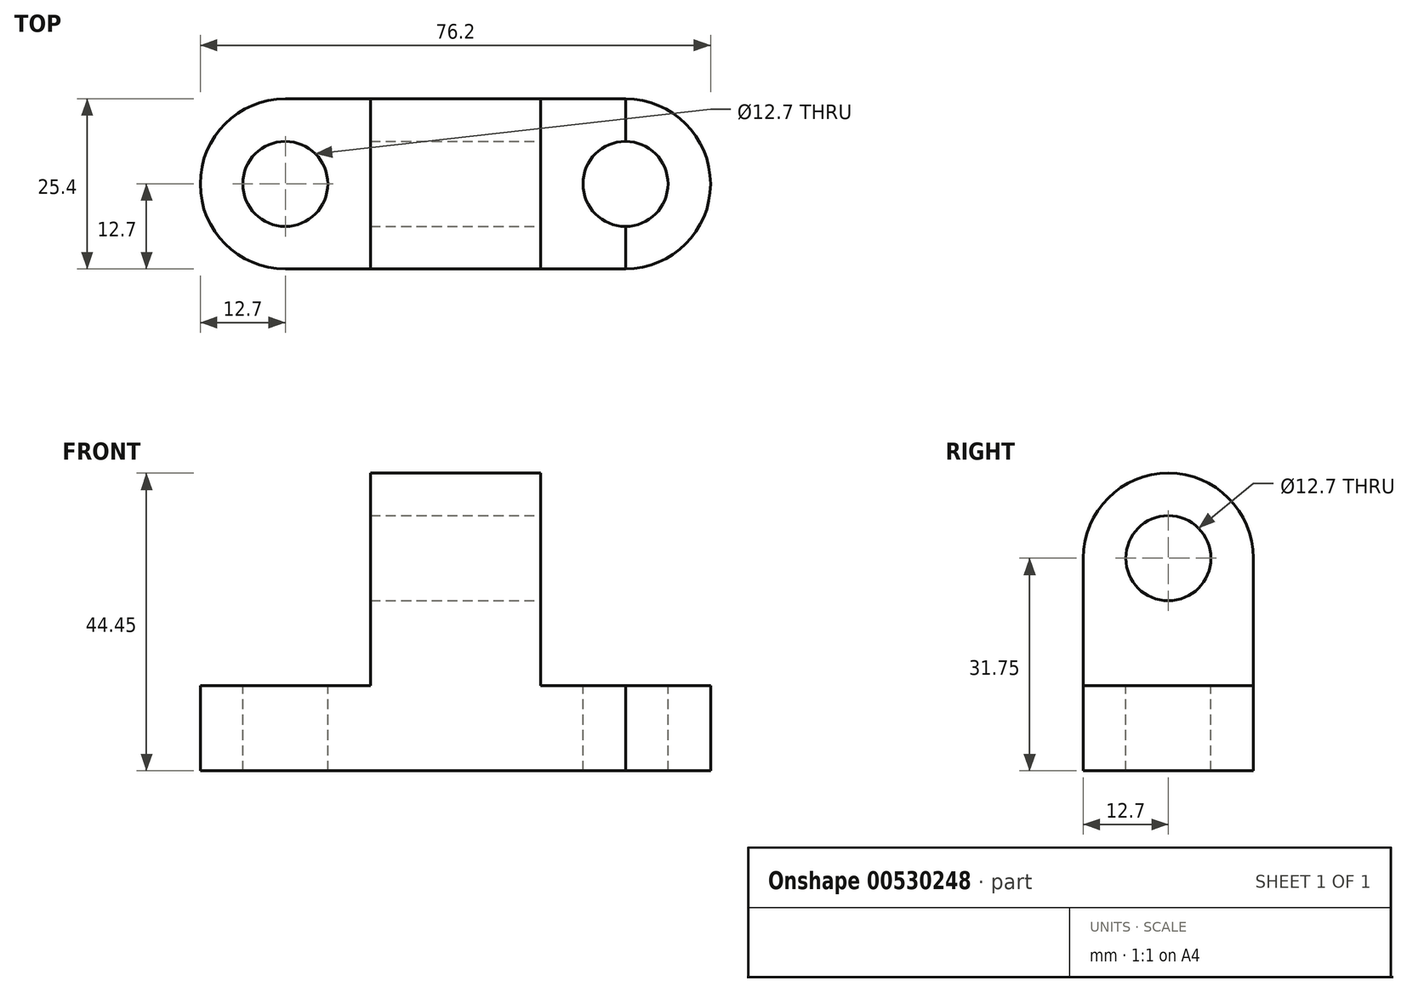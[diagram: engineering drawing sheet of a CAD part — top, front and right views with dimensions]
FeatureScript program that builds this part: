
annotation { "Feature Type Name" : "Feature", "Feature Type Description" : "" }
export const myFeature = defineFeature(function(context is Context, id is Id, definition is map)
    precondition{}
    {
        {
            var Q0;
            Q0=qCreatedBy(makeId("Front.planeOp"),FACE);
            var sketch = newSketch(context, id + "F0", { "sketchPlane" : qUnion([Q0])});
            skLineSegment(sketch, "E0", {"start": v(-77.55, 0) * mm, "end": v(-26.75, 0) * mm});
            skLineSegment(sketch, "E1", {"start": v(-26.75, 0) * mm, "end": v(-26.75, 12.7) * mm});
            skLineSegment(sketch, "E2", {"start": v(-26.75, 12.7) * mm, "end": v(-39.45, 12.7) * mm});
            skLineSegment(sketch, "E3", {"start": v(-39.45, 12.7) * mm, "end": v(-39.45, 31.75) * mm});
            skLineSegment(sketch, "E4", {"start": v(-39.45, 31.75) * mm, "end": v(-64.85, 31.75) * mm});
            skLineSegment(sketch, "E5", {"start": v(-64.85, 31.75) * mm, "end": v(-64.85, 12.7) * mm});
            skLineSegment(sketch, "E6", {"start": v(-64.85, 12.7) * mm, "end": v(-77.55, 12.7) * mm});
            skLineSegment(sketch, "E7", {"start": v(-77.55, 12.7) * mm, "end": v(-77.55, 0) * mm});
            skSolve(sketch);
        }
        {
            var Q0;
            Q0 = qSketchRegion(id + "F0", true);
            extrude(context, id + "F1", {"entities" : qUnion([Q0]), "depth" : 25.4 * mm, "offsetDistance" : 25.4 * mm});
        }
        {
            var Q0;
            Q0=makeQuery(id+"F1.opExtrude","SWEPT_FACE",FACE,{"disambiguationData":[OSD([sQuery(id+"F0.wireOp",EDGE,"E2")])]});
            var sketch = newSketch(context, id + "F2", { "sketchPlane" : qUnion([Q0])});
            skArc(sketch, "E8", {"start": v(-26.75, -25.4) * mm, "mid": v(-14.05, -12.7) * mm, "end": v(-26.75, 0) * mm});
            skSolve(sketch);
        }
        {
            var Q0;
            Q0 = qSketchRegion(id + "F2", true);
            var Q1;
            Q1=makeQuery(id+"F2.imprint","IMPRINT",FACE,{"disambiguationData":[TD([[makeQuery(id+"F2.imprint","IMPRINT",EDGE,{"derivedFrom":sQuery(id+"F2.wireOp",EDGE,"E8")}),1.0]])]});
            extrude(context, id + "F3", {"entities" : qUnion([Q0, Q1]), "oppositeDirection" : true, "depth" : 12.7 * mm, "offsetDistance" : 25.4 * mm});
        }
        {
            var Q0;
            Q0=makeQuery(id+"F1.opExtrude","SWEPT_FACE",FACE,{"disambiguationData":[OSD([sQuery(id+"F0.wireOp",EDGE,"E6")])]});
            var sketch = newSketch(context, id + "F4", { "sketchPlane" : qUnion([Q0])});
            skArc(sketch, "E9", {"start": v(-77.55, 0) * mm, "mid": v(-90.25, -12.7) * mm, "end": v(-77.55, -25.4) * mm});
            skSolve(sketch);
        }
        {
            var Q0;
            Q0 = qSketchRegion(id + "F4", true);
            var Q1;
            Q1=makeQuery(id+"F4.imprint","IMPRINT",FACE,{"disambiguationData":[TD([[makeQuery(id+"F4.imprint","IMPRINT",EDGE,{"derivedFrom":sQuery(id+"F4.wireOp",EDGE,"E9")}),1.0]])]});
            extrude(context, id + "F5", {"entities" : qUnion([Q0, Q1]), "operationType" : NewBodyOperationType.ADD, "oppositeDirection" : true, "depth" : 12.7 * mm, "offsetDistance" : 25.4 * mm});
        }
        {
            var Q0;
            Q0=makeQuery(id+"F1.opExtrude","SWEPT_FACE",FACE,{"disambiguationData":[OSD([sQuery(id+"F0.wireOp",EDGE,"E3")])]});
            var sketch = newSketch(context, id + "F6", { "sketchPlane" : qUnion([Q0])});
            skArc(sketch, "E10", {"start": v(0, 31.75) * mm, "mid": v(-12.7, 44.45) * mm, "end": v(-25.4, 31.75) * mm});
            skSolve(sketch);
        }
        {
            var Q0;
            Q0=makeQuery(id+"F6.imprint","IMPRINT",FACE,{"disambiguationData":[TD([[makeQuery(id+"F6.imprint","IMPRINT",EDGE,{"derivedFrom":sQuery(id+"F6.wireOp",EDGE,"E10")}),1.0]])]});
            var Q1;
            Q1 = qSketchRegion(id + "F4", true);
            extrude(context, id + "F7", {"entities" : qUnion([Q0, Q1]), "operationType" : NewBodyOperationType.ADD, "oppositeDirection" : true, "depth" : 25.4 * mm, "offsetDistance" : 25.4 * mm});
        }
        {
            var Q0;
            {var subQ0=sQuery(id+"F0.wireOp",EDGE,"E6");Q0=makeQuery(id+"F5.boolean.opBoolean","MERGE",FACE,{"derivedFrom":[makeQuery(id+"F1.opExtrude","SWEPT_FACE",FACE,{"disambiguationData":[OSD([subQ0])]}),makeQuery(id+"F5.opExtrude","CAP_FACE",FACE,{"disambiguationData":[OSD([subQ0,sQuery(id+"F0.wireOp",EDGE,"E7"),sQuery(id+"F4.wireOp",EDGE,"E9")])],"isStart":true})]});}
            var sketch = newSketch(context, id + "F8", { "sketchPlane" : qUnion([Q0])});
            skCircle(sketch, "E11", {"center": v(-77.55, -12.7) * mm, "radius": 6.35 * mm});
            skSolve(sketch);
        }
        {
            var Q0;
            Q0=makeQuery(id+"F8.imprint","IMPRINT",FACE,{"disambiguationData":[TD([[makeQuery(id+"F8.imprint","IMPRINT",EDGE,{"derivedFrom":sQuery(id+"F8.wireOp",EDGE,"E11")}),1.0]])]});
            extrude(context, id + "F9", {"entities" : qUnion([Q0]), "operationType" : NewBodyOperationType.REMOVE, "oppositeDirection" : true, "depth" : 25.4 * mm, "offsetDistance" : 25.4 * mm});
        }
        {
            var Q0;
            Q0=makeQuery(id+"F1.opExtrude","SWEPT_FACE",FACE,{"disambiguationData":[OSD([sQuery(id+"F0.wireOp",EDGE,"E2")])]});
            var sketch = newSketch(context, id + "F10", { "sketchPlane" : qUnion([Q0])});
            skCircle(sketch, "E12", {"center": v(-26.75, -12.7) * mm, "radius": 6.35 * mm});
            skSolve(sketch);
        }
        {
            var Q0;
            {var subQ0=sQuery(id+"F10.wireOp",EDGE,"E12");var subQ1=makeQuery(id+"F1.opExtrude","SWEPT_EDGE",EDGE,{"disambiguationData":[OSD([sQuery(id+"F0.wireOp",EDGE,"E1"),sQuery(id+"F0.wireOp",EDGE,"E2")])]});var subQ2=makeQuery(id+"F10.imprint","INTERSECT",VERTEX,{"disambiguationData":[OD(0.0)],"derivedFrom":[subQ1,subQ0]});Q0=makeQuery(id+"F10.imprint","IMPRINT",FACE,{"disambiguationData":[TD([[makeQuery(id+"F10.imprint","IMPRINT",EDGE,{"disambiguationData":[TD([[subQ2,1.0]])],"derivedFrom":subQ0}),1.0]])]});}
            var Q1;
            {var subQ0=sQuery(id+"F10.wireOp",EDGE,"E12");var subQ1=makeQuery(id+"F1.opExtrude","SWEPT_EDGE",EDGE,{"disambiguationData":[OSD([sQuery(id+"F0.wireOp",EDGE,"E1"),sQuery(id+"F0.wireOp",EDGE,"E2")])]});var subQ2=makeQuery(id+"F10.imprint","INTERSECT",VERTEX,{"disambiguationData":[OD(0.0)],"derivedFrom":[subQ1,subQ0]});Q1=makeQuery(id+"F10.imprint","IMPRINT",FACE,{"disambiguationData":[TD([[makeQuery(id+"F10.imprint","IMPRINT",EDGE,{"disambiguationData":[TD([[subQ2,-1.0]])],"derivedFrom":subQ0}),1.0]])]});}
            extrude(context, id + "F11", {"entities" : qUnion([Q0, Q1]), "operationType" : NewBodyOperationType.REMOVE, "oppositeDirection" : true, "depth" : 25.4 * mm, "offsetDistance" : 25.4 * mm});
        }
        {
            var Q0;
            {var subQ0=sQuery(id+"F10.wireOp",EDGE,"E12");var subQ1=makeQuery(id+"F1.opExtrude","SWEPT_EDGE",EDGE,{"disambiguationData":[OSD([sQuery(id+"F0.wireOp",EDGE,"E1"),sQuery(id+"F0.wireOp",EDGE,"E2")])]});var subQ2=makeQuery(id+"F10.imprint","INTERSECT",VERTEX,{"disambiguationData":[OD(0.0)],"derivedFrom":[subQ1,subQ0]});Q0=makeQuery(id+"F10.imprint","IMPRINT",FACE,{"disambiguationData":[TD([[makeQuery(id+"F10.imprint","IMPRINT",EDGE,{"disambiguationData":[TD([[subQ2,-1.0]])],"derivedFrom":subQ0}),1.0]])]});}
            extrude(context, id + "F12", {"entities" : qUnion([Q0]), "operationType" : NewBodyOperationType.REMOVE, "oppositeDirection" : true, "depth" : 25.4 * mm, "offsetDistance" : 25.4 * mm});
        }
        {
            var Q0;
            {var subQ0=sQuery(id+"F0.wireOp",EDGE,"E3");Q0=makeQuery(id+"F7.boolean.opBoolean","MERGE",FACE,{"derivedFrom":[makeQuery(id+"F1.opExtrude","SWEPT_FACE",FACE,{"disambiguationData":[OSD([subQ0])]}),makeQuery(id+"F7.opExtrude","CAP_FACE",FACE,{"disambiguationData":[OSD([subQ0,sQuery(id+"F0.wireOp",EDGE,"E4"),sQuery(id+"F6.wireOp",EDGE,"E10")])],"isStart":true})]});}
            var sketch = newSketch(context, id + "F13", { "sketchPlane" : qUnion([Q0])});
            skCircle(sketch, "E13", {"center": v(-12.7, 31.75) * mm, "radius": 6.35 * mm});
            skSolve(sketch);
        }
        {
            var Q0;
            Q0 = qSketchRegion(id + "F13", true);
            extrude(context, id + "F14", {"entities" : qUnion([Q0]), "operationType" : NewBodyOperationType.REMOVE, "oppositeDirection" : true, "depth" : 25.4 * mm, "offsetDistance" : 25.4 * mm});
        }
    });
